# Revit family: PRD_FrankeWS_WCFlshngVlvs_WCFlushingValve_AQRM550
name_source: partatom
category: Plumbing Fixtures
revit_build: Autodesk Revit 2018 (Build: 20190510_1515(x64)
units: mm (PartAtom-declared; Revit-internal decimal feet)

## family parameters
Always vertical = Yes
Cut with Voids When Loaded = No
OmniClass Number = 23.45.05.14.99
OmniClass Title = Other Sanitary Washing Plumbing Fixtures
Part Type = Normal
Room Calculation Point = No
Round Connector Dimension = Use Diameter
Shared = No
Work Plane-Based = Yes

## types (1)
- AQRM550
    AssetType = Fixed
    BIMObjectName = PRD_AR_WCFlushingValves_WCFlushingValve_AQRM550
    CalculationFlowRateColdWater = 1.00 liter per second
    Category = Pr_40_20_93_91, WC flushing valves
    Default Elevation = 1219 mm
    Description = AQUAREX WC flush valve DN 20, noise group I, for surface installation, with automatic volume flow control and adjustable flushing water volume, in polished chromium-plated brass, push cap and screw fitting made of metal.
    DiameterNominal = 20  [stored 0.0656168 ft]
    DurationUnit = year
    Features = in polished chromium-plated brass, push cap and screw fitting made of metal
    Finish = chromed
    FlowColdWater = 1.0 L/s
    FlushValveMaterial = PRD_AR_ChromatedBrass_HighPolished
    FlushingRate = 1.3 L/s
    FunctionalPrinciple = Hydraulic self-closing
    GrossWeight = 1.26 kg
    HasIntegralShutOffDevice = Yes
    IfcExportAs = IfcValveType
    IfcExportType = FLUSHING
    IsHighPressure = No
    Manufacturer = KWC Group AG
    ManufacturerName = KWC Group AG
    ManufacturerURL = www.kwc.com
    Material = brass
    MaximumFlowPressure = 4.00 bar
    MaximumFlushWaterVolume = 9.00 liter
    MaximumFlushingFlow = 1.30 liter per second
    MinimumFlowPressure = 1.20 bar
    MinimumFlushWaterVolume = 6.00 liter
    MinimumFlushingFlow = 1.00 liter per second
    Model = AQRM550
    ModelNumber = 2000100076
    ModelReference = AQRM550
    NBSDescription = WC flushing valves
    NBSReference = 45-35-70/389
    Name = WC flushing valve AQRM550
    NetWeight = 1.20 kg
    NominalDepth = 0 mm  [stored 0 ft]
    NominalHeight = 0 mm  [stored 0 ft]
    NominalWidth = 0 mm  [stored 0 ft]
    OutletSize = DN-20-3-4INH
    ProductInformation = https://pim.kwc.com
    ProtectiveShutdown = No
    SoundInsulation = 1
    SurfaceFinishFitting = Chromed
    TypeOfFlushingFitting = WC flush valve
    TypeOfMounting = Wall mounting
    TypeOfOperation = Manual operation
    URL = www.kwc.com
    Uniclass2015Code = Pr_40_20_93_91
    Uniclass2015Title = WC flushing valves
    Uniclass2015Version = Products v1.17
    Version = 1
    WarrantyDurationUnit = year

note: [stored X ft] marks values corroborated as IEEE doubles in the binary element streams (Revit-internal decimal feet)

## geometry (parser evidence)
native form markers: Sweep x3
no freeform markers — native parametric forms only
